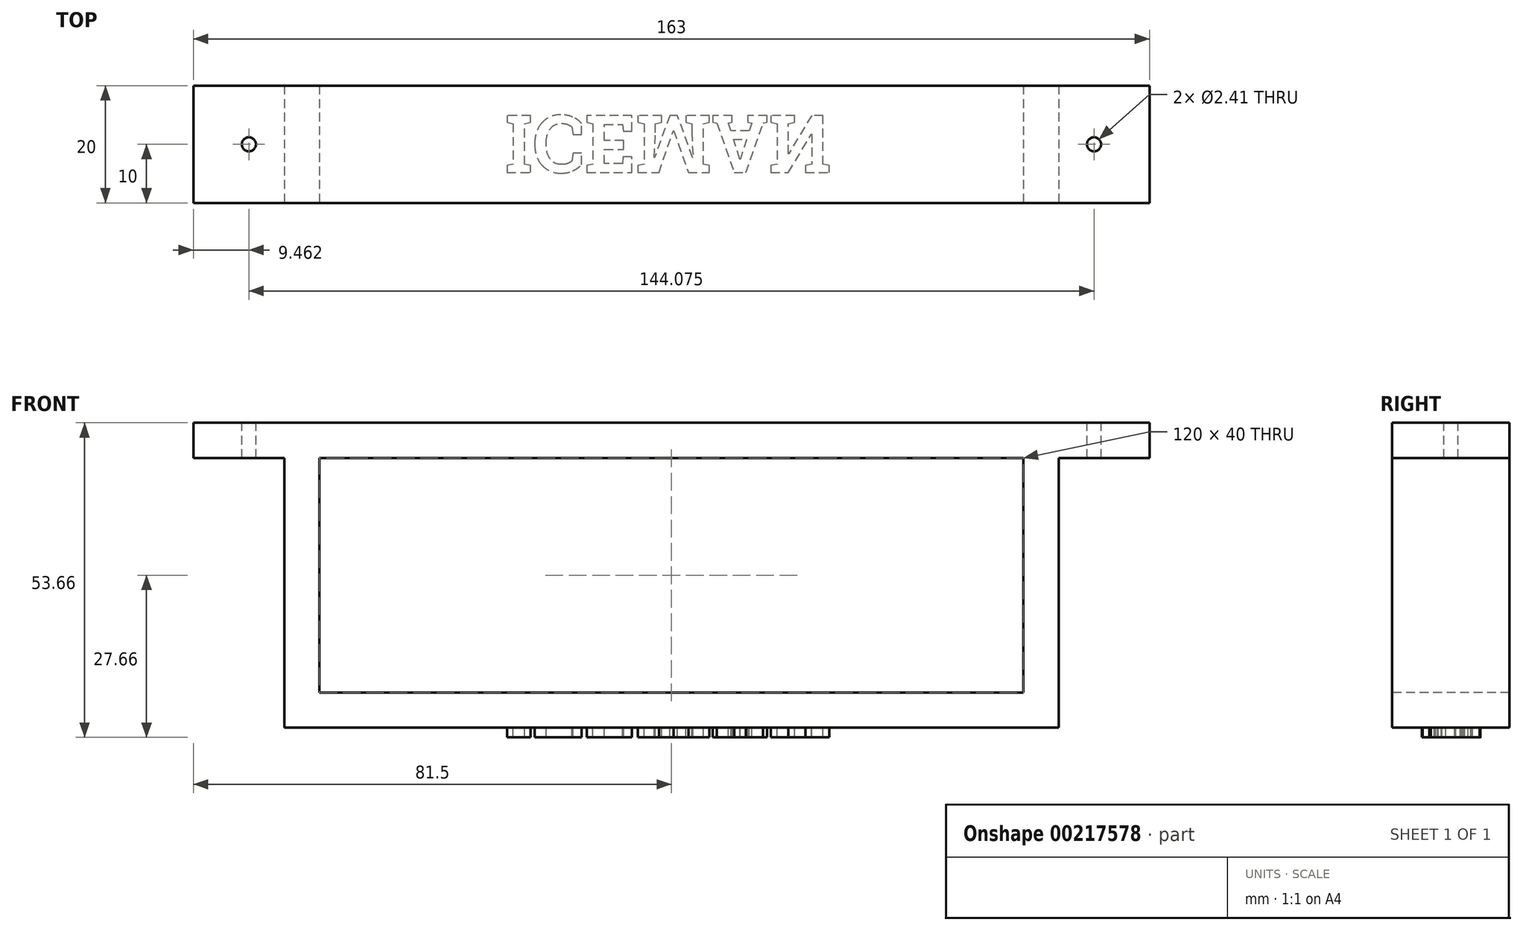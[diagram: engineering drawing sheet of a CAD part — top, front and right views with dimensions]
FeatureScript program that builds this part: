
annotation { "Feature Type Name" : "Feature", "Feature Type Description" : "" }
export const myFeature = defineFeature(function(context is Context, id is Id, definition is map)
    precondition{}
    {
        {
            var Q0;
            Q0=qCreatedBy(makeId("Top.planeOp"),FACE);
            var sketch = newSketch(context, id + "F0", { "sketchPlane" : qUnion([Q0])});
            skLineSegment(sketch, "E0.bottom", {"start": v(-66, 10) * mm, "end": v(66, 10) * mm});
            skLineSegment(sketch, "E0.top", {"start": v(-66, -10) * mm, "end": v(66, -10) * mm});
            skLineSegment(sketch, "E0.left", {"start": v(-66, 10) * mm, "end": v(-66, -10) * mm});
            skLineSegment(sketch, "E0.right", {"start": v(66, 10) * mm, "end": v(66, -10) * mm});
            skPoint(sketch, "E0.middle", {"position": v(0, 0) * mm});
            skSolve(sketch);
        }
        {
            var Q0;
            Q0=makeQuery(id+"F0.imprint","IMPRINT",FACE,{"disambiguationData":[TD([[makeQuery(id+"F0.imprint","IMPRINT",EDGE,{"derivedFrom":sQuery(id+"F0.wireOp",EDGE,"E0.bottom")}),-1.0]])]});
            extrude(context, id + "F1", {"entities" : qUnion([Q0]), "depth" : 6 * mm});
        }
        {
            var Q0;
            Q0=makeQuery(id+"F1.opExtrude","CAP_FACE",FACE,{"disambiguationData":[OSD([sQuery(id+"F0.wireOp",EDGE,"E0.bottom"),sQuery(id+"F0.wireOp",EDGE,"E0.top"),sQuery(id+"F0.wireOp",EDGE,"E0.left"),sQuery(id+"F0.wireOp",EDGE,"E0.right")])],"isStart":false});
            var sketch = newSketch(context, id + "F2", { "sketchPlane" : qUnion([Q0])});
            skLineSegment(sketch, "E1.bottom", {"start": v(-66, 10) * mm, "end": v(-60, 10) * mm});
            skLineSegment(sketch, "E1.top", {"start": v(-66, -10) * mm, "end": v(-60, -10) * mm});
            skLineSegment(sketch, "E1.left", {"start": v(-66, 10) * mm, "end": v(-66, -10) * mm});
            skLineSegment(sketch, "E1.right", {"start": v(-60, 10) * mm, "end": v(-60, -10) * mm});
            skLineSegment(sketch, "E2.bottom", {"start": v(66, 10) * mm, "end": v(60, 10) * mm});
            skLineSegment(sketch, "E2.top", {"start": v(66, -10) * mm, "end": v(60, -10) * mm});
            skLineSegment(sketch, "E2.left", {"start": v(66, 10) * mm, "end": v(66, -10) * mm});
            skLineSegment(sketch, "E2.right", {"start": v(60, 10) * mm, "end": v(60, -10) * mm});
            skSolve(sketch);
        }
        {
            var Q0;
            Q0 = qSketchRegion(id + "F2", true);
            extrude(context, id + "F3", {"entities" : qUnion([Q0]), "operationType" : NewBodyOperationType.ADD, "depth" : 40 * mm});
        }
        {
            var Q0;
            Q0=makeQuery(id+"F3.opExtrude","CAP_FACE",FACE,{"disambiguationData":[OSD([sQuery(id+"F2.wireOp",EDGE,"E1.bottom"),sQuery(id+"F2.wireOp",EDGE,"E1.top"),sQuery(id+"F2.wireOp",EDGE,"E1.left"),sQuery(id+"F2.wireOp",EDGE,"E1.right")])],"isStart":false});
            var sketch = newSketch(context, id + "F4", { "sketchPlane" : qUnion([Q0])});
            skLineSegment(sketch, "E3.bottom", {"start": v(-81.5, 10) * mm, "end": v(81.5, 10) * mm});
            skLineSegment(sketch, "E3.top", {"start": v(-81.5, -10) * mm, "end": v(81.5, -10) * mm});
            skLineSegment(sketch, "E3.left", {"start": v(-81.5, 10) * mm, "end": v(-81.5, -10) * mm});
            skLineSegment(sketch, "E3.right", {"start": v(81.5, 10) * mm, "end": v(81.5, -10) * mm});
            skPoint(sketch, "E3.middle", {"position": v(0, 0) * mm});
            skSolve(sketch);
        }
        {
            var Q0;
            {var subQ2=sQuery(id+"F4.wireOp",EDGE,"E3.right");Q0=makeQuery(id+"F4.imprint","IMPRINT",FACE,{"disambiguationData":[TD([[makeQuery(id+"F4.imprint","IMPRINT",EDGE,{"derivedFrom":subQ2}),-1.0]])]});}
            var Q1;
            {var subQ1=makeQuery(id+"F3.opExtrude","CAP_EDGE",EDGE,{"disambiguationData":[OSD([sQuery(id+"F2.wireOp",EDGE,"E1.left")])],"isStart":false});Q1=makeQuery(id+"F4.imprint","IMPRINT",FACE,{"disambiguationData":[TD([[makeQuery(id+"F4.imprint","IMPRINT",EDGE,{"derivedFrom":subQ1}),1.0]])]});}
            var Q2;
            {var subQ2=sQuery(id+"F4.wireOp",EDGE,"E3.left");Q2=makeQuery(id+"F4.imprint","IMPRINT",FACE,{"disambiguationData":[TD([[makeQuery(id+"F4.imprint","IMPRINT",EDGE,{"derivedFrom":subQ2}),1.0]])]});}
            extrude(context, id + "F5", {"entities" : qUnion([Q0, Q1, Q2]), "operationType" : NewBodyOperationType.ADD, "depth" : 6 * mm});
        }
        {
            var Q0;
            Q0=makeQuery(id+"F5.opExtrude","CAP_FACE",FACE,{"disambiguationData":[OSD([sQuery(id+"F4.wireOp",EDGE,"E3.bottom"),sQuery(id+"F4.wireOp",EDGE,"E3.top"),sQuery(id+"F4.wireOp",EDGE,"E3.left"),sQuery(id+"F4.wireOp",EDGE,"E3.right")])],"isStart":false});
            var sketch = newSketch(context, id + "F6", { "sketchPlane" : qUnion([Q0])});
            skLineSegment(sketch, "E4.bottom", {"start": v(-72.04, -2.52) * mm, "end": v(72.04, -2.52) * mm, "construction": true});
            skLineSegment(sketch, "E4.top", {"start": v(-72.04, 2.52) * mm, "end": v(72.04, 2.52) * mm, "construction": true});
            skLineSegment(sketch, "E4.left", {"start": v(-72.04, -2.52) * mm, "end": v(-72.04, 2.52) * mm, "construction": true});
            skLineSegment(sketch, "E4.right", {"start": v(72.04, -2.52) * mm, "end": v(72.04, 2.52) * mm, "construction": true});
            skPoint(sketch, "E4.middle", {"position": v(0, 0) * mm});
            skCircle(sketch, "E5", {"center": v(-72.04, 0) * mm, "radius": 1.2 * mm});
            skCircle(sketch, "E6", {"center": v(72.04, 0) * mm, "radius": 1.2 * mm});
            skSolve(sketch);
        }
        {
            var Q0;
            Q0 = qSketchRegion(id + "F6", true);
            extrude(context, id + "F7", {"entities" : qUnion([Q0]), "operationType" : NewBodyOperationType.REMOVE, "endBound" : BoundingType.THROUGH_ALL, "oppositeDirection" : true, "depth" : 25 * mm});
        }
        {
            var Q0;
            Q0=makeQuery(id+"F1.opExtrude","CAP_FACE",FACE,{"disambiguationData":[OSD([sQuery(id+"F0.wireOp",EDGE,"E0.bottom"),sQuery(id+"F0.wireOp",EDGE,"E0.top"),sQuery(id+"F0.wireOp",EDGE,"E0.left"),sQuery(id+"F0.wireOp",EDGE,"E0.right")])],"isStart":true});
            var sketch = newSketch(context, id + "F8", { "sketchPlane" : qUnion([Q0])});
            skText(sketch, "E7", { "text": "ICEMAN", "fontName": "RobotoSlab-Bold.ttf"});
            const initialGuessF8  = {"E7": [-0.0284, -0.00491, 1, 0, 0.00983]};
            skSetInitialGuess(sketch, initialGuessF8);
            skSolve(sketch);
        }
        {
            var Q0;
            Q0=makeQuery(id+"F8.imprint","IMPRINT",FACE,{"disambiguationData":[TD([[makeQuery(id+"F8.imprint","IMPRINT",EDGE,{"derivedFrom":sQuery(id+"F8.wireOp",EDGE,"E7.sketch_text.stroke-0")}),-1.0]])]});
            var Q1;
            Q1=makeQuery(id+"F8.imprint","IMPRINT",FACE,{"disambiguationData":[TD([[makeQuery(id+"F8.imprint","IMPRINT",EDGE,{"derivedFrom":sQuery(id+"F8.wireOp",EDGE,"E7.sketch_text.stroke-12")}),-1.0]])]});
            var Q2;
            Q2=makeQuery(id+"F8.imprint","IMPRINT",FACE,{"disambiguationData":[TD([[makeQuery(id+"F8.imprint","IMPRINT",EDGE,{"derivedFrom":sQuery(id+"F8.wireOp",EDGE,"E7.sketch_text.stroke-36")}),-1.0]])]});
            var Q3;
            Q3=makeQuery(id+"F8.imprint","IMPRINT",FACE,{"disambiguationData":[TD([[makeQuery(id+"F8.imprint","IMPRINT",EDGE,{"derivedFrom":sQuery(id+"F8.wireOp",EDGE,"E7.sketch_text.stroke-57")}),-1.0]])]});
            var Q4;
            Q4=makeQuery(id+"F8.imprint","IMPRINT",FACE,{"disambiguationData":[TD([[makeQuery(id+"F8.imprint","IMPRINT",EDGE,{"derivedFrom":sQuery(id+"F8.wireOp",EDGE,"E7.sketch_text.stroke-108")}),-1.0]])]});
            var Q5;
            Q5=makeQuery(id+"F8.imprint","IMPRINT",FACE,{"disambiguationData":[TD([[makeQuery(id+"F8.imprint","IMPRINT",EDGE,{"derivedFrom":sQuery(id+"F8.wireOp",EDGE,"E7.sketch_text.stroke-88")}),-1.0]])]});
            extrude(context, id + "F9", {"entities" : qUnion([Q0, Q1, Q2, Q3, Q4, Q5]), "operationType" : NewBodyOperationType.ADD, "depth" : 1.66 * mm});
        }
    });
